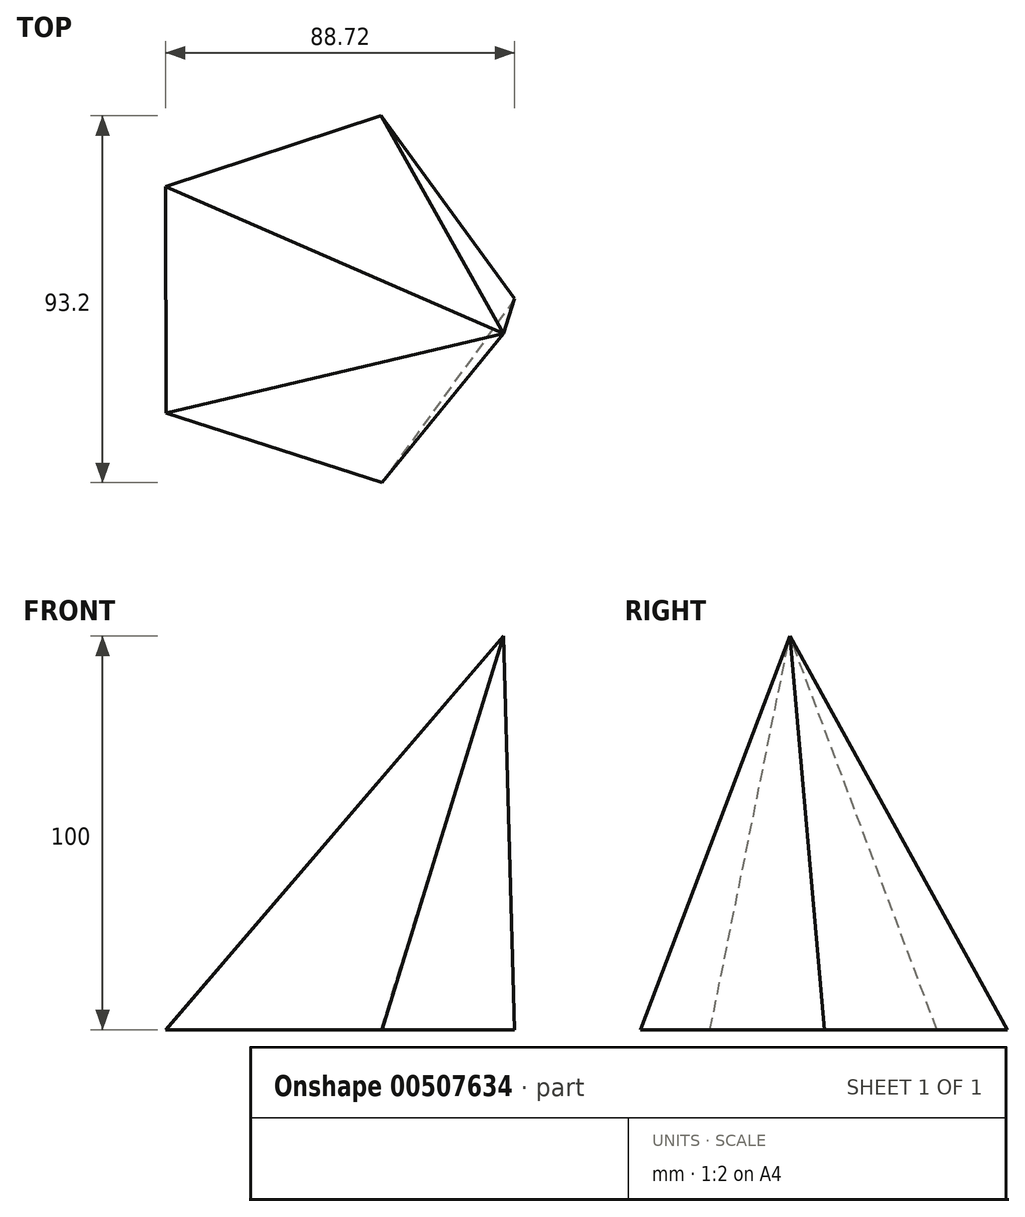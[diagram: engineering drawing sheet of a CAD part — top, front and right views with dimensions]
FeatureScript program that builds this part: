
annotation { "Feature Type Name" : "Feature", "Feature Type Description" : "" }
export const myFeature = defineFeature(function(context is Context, id is Id, definition is map)
    precondition{}
    {
        {
            var Q0;
            Q0=qCreatedBy(makeId("Top.planeOp"),FACE);
            var sketch = newSketch(context, id + "F0", { "sketchPlane" : qUnion([Q0])});
            skCircle(sketch, "E0.cCircle", {"center": v(4.32, 0) * mm, "radius": 49 * mm, "construction": true});
            skLineSegment(sketch, "E0.0", {"start": v(19.58, -46.56) * mm, "end": v(-35.25, -28.9) * mm});
            skLineSegment(sketch, "E0.1", {"start": v(-35.25, -28.9) * mm, "end": v(-35.4, 28.7) * mm});
            skLineSegment(sketch, "E0.2", {"start": v(-35.4, 28.7) * mm, "end": v(19.34, 46.64) * mm});
            skLineSegment(sketch, "E0.3", {"start": v(19.34, 46.64) * mm, "end": v(53.32, 0.13) * mm});
            skLineSegment(sketch, "E0.4", {"start": v(53.32, 0.13) * mm, "end": v(19.58, -46.56) * mm});
            skSolve(sketch);
        }
        {
            var Q0;
            Q0=qCreatedBy(makeId("Top.planeOp"),FACE);
            cPlane(context, id + "F1", {"entities" : qUnion([Q0]), "cplaneType" : CPlaneType.OFFSET, "offset" : 100 * mm, "width" : 152.4 * mm, "height" : 152.4 * mm});
        }
        {
            var Q0;
            Q0=qCreatedBy(id+"F1.planeOp",FACE);
            var sketch = newSketch(context, id + "F2", { "sketchPlane" : qUnion([Q0])});
            skPoint(sketch, "E1", {"position": v(50.48, -8.68) * mm});
            skSolve(sketch);
        }
        {
            var Q0;
            Q0=makeQuery(id+"F0.imprint","IMPRINT",FACE,{"disambiguationData":[TD([[makeQuery(id+"F0.imprint","IMPRINT",EDGE,{"derivedFrom":sQuery(id+"F0.wireOp",EDGE,"E0.0")}),-1.0]])]});
            var Q1;
            Q1=sQuery(id+"F2.wireOp",VERTEX,"E1");
            loft(context, id + "F3", {"sheetProfilesArray" : [{ "sheetProfileEntities" : qUnion([Q0]) }, { "sheetProfileEntities" : qUnion([Q1]) }]});
        }
    });
